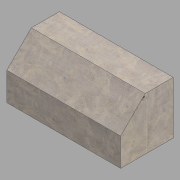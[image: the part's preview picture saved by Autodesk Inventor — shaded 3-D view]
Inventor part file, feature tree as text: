
AUTODESK INVENTOR PART (.ipt)
format: ipt  version: 2022.2 (Build 262287000, 287)  size: 126,464 bytes
history: native  units: in
note: dims shown in document units (in); Inventor stores cm internally (conversion verified against a paired STEP export)
features: extrude x1, sketch x1
ambient origin geometry x8: Origin, YZ Plane, XZ Plane, XY Plane, X Axis, Y Axis, Z Axis, Center Point
bodies: Solid1 (feature_tree)
feature tree (2):
  extrude  "Extrusion1"  Depth=7.5in
  sketch  "Sketch1"  dims[d0=7.5in d1=7.5in d2=4.0in d3=4.0in d4=3.5in d5=3.5in d6=16.25in d7=0.0in]
